# Revit family: Chair-Soft_Seating-Allermuir-Haven_Bench-HAB300BM
name_source: partatom
category: Furniture
revit_build: Autodesk Revit MEP 2012 (Build: 20110309_2315)
units: mm (PartAtom-declared; Revit-internal decimal feet)

## types (1)
- HAB300BM
    04 CSI = 12 51 00
    95 CSI = 12510
    Assembly Code = E2020200
    Back = Fabric - Allermuir - Upholstery - Velvet - Red
    Base = Plastic - Allermuir - Black
    Color Availability = See price list for material options
    Depth = 0' - 0"
    Fabric Spec Sheets = http://www.allermuir.net
    Height = 0' - 0"
    Manufacturer = Allermuir
    Manufacturer Fax = (419) 887 5805
    Model = HAB300BM
    Plastic Arms in Black = No
    Plugin Data URL = http://products.ecoscorecard.com
    Product Line = Haven Bench
    Product Page URL = http://www.allermuir.net
    Seat or Top = Fabric - Allermuir - Silcoates
    Side Bracket = Metal - Allermuir - Chrome - Polished
    Stacks = No
    Subcategory = Soft Seating
    URL = http://www.allermuir.net
    Upholstered Back = No
    Upholstered Seat = No
    Weight = 0.0 lb
    Width = 0' - 0"
    ecoScorecard Product Page = http://products.ecoscorecard.com
    ecoScorecard_data = http://thesenatorgroup.ecoscorecard.com

## geometry (parser evidence)
native form markers: Sweep x8
no freeform markers — native parametric forms only
